# Revit family: Leviton_CATSTD-LP6XX-MB-D01
name_source: partatom
category: Electrical Equipment
units: mm (PartAtom-declared; Revit-internal decimal feet)

## family parameters
Always vertical = Yes
Cut with Voids When Loaded = Yes
Host = Wall
Maintain Annotation Orientation = No
Panel Configuration = Two Columns, Circuits Across
Part Type = Panelboard
Room Calculation Point = No
Round Connector Dimension = Use Diameter
Shared = No

## types (2) — shared parameters
Cost = 1 $
Dimensions = 55.873" H x 14.248" W x 3.975" D
Ground Bus = No
Manufacturer = Leviton
NEMA Enclosure Type = NEMA 1 Indoor
Neutral Bus = No
Neutral Rating = 0.00%
Product Data = https://www.arcat.com
Specification = https://www.arcat.com
URL = https://www.leviton.com
Unit Depth = 3.975 "
Unit Height = 55.873 "
Unit Width = 14.248 "
Voltage_MEP = 120 V
Weight = 53.00 lbf
zero-valued in all types: Default Elevation

## per-type parameters (varying)
| type | Description | Model |
| LP622-MB 225A | 66 Space Indoor Load Center with 225A Main Circuit Breaker | LP622-MB 225 |
| LP622-MB 200A | 66 Space Indoor Load Center with 200A Main Circuit Breaker | LP622-MB 200 |

## geometry (parser evidence)
native form markers: Sweep x5
no freeform markers — native parametric forms only
